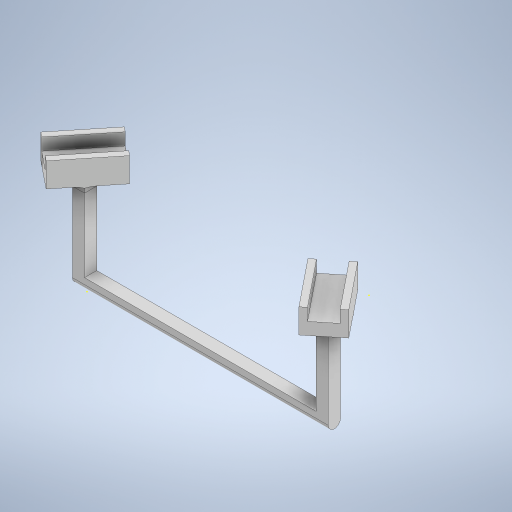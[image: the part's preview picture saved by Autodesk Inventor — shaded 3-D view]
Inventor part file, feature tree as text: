
AUTODESK INVENTOR PART (.ipt)
format: ipt  version: 2023 (Build 270158000, 158)  size: 727,040 bytes
history: native  units: in
note: dims shown in document units (in); Inventor stores cm internally (conversion verified against a paired STEP export)
features: sketch x13, extrude x10, fillet x2
ambient origin geometry x8: Origin, YZ Plane, XZ Plane, XY Plane, X Axis, Y Axis, Z Axis, Center Point
bodies: Solid1 (feature_tree)
feature tree (25):
  extrude  "Extrusion1"  Depth=0.25in
  fillet  "Fillet1"  Radius=1.75in
  extrude  "Extrusion2"  Depth=5.25in
  sketch  "Sketch4"  dims[d6=0.25in d7=0.0in d8=0.125in]
  sketch  "Sketch5"  dims[d11=0.25in d12=0.0in d32=0.0625in d33=0.0in]
  extrude  "Extrusion3"  Depth=0.125in
  extrude  "Extrusion4"  Depth=0.25in TaperAngle=0.0deg
  extrude  "Extrusion5"  Depth=0.0625in TaperAngle=0.0deg
  extrude  "Extrusion6"  Depth=0.5in
  sketch  "Sketch10"  dims[d48=0.125in d49=0.0in d50=0.25in]
  extrude  "Extrusion7"  Depth=0.125in TaperAngle=0.0deg
  extrude  "Extrusion8"  Depth=0.125in TaperAngle=0.0deg
  extrude  "Extrusion9"  Depth=0.25in
  extrude  "Extrusion10"  TaperAngle=0.0deg  [1 undecoded]
  fillet  "Fillet4"  Radius=0.5in
  sketch  "Sketch1"  dims[d1=2.0in d2=0.25in d3=1.75in]
  sketch  "Sketch2"  dims[d4=4.75in d5=5.25in]
  sketch  "Sketch6"  dims[d34=0.0625in d35=0.0in d36=0.0625in d37=0.0in]
  sketch  "Sketch7"  dims[d38=0.0625in d39=0.0in d40=0.5in]
  sketch  "Sketch8"  dims[d41=0.125in d42=0.0in d43=0.125in d44=0.0in]
  sketch  "Sketch9"  dims[d45=0.5in d46=0.125in d47=0.0in]
  sketch  "Sketch11"  dims[d9=0.0in d10=0.0in d27=0.5in]
  sketch  "Sketch12"  dims[d28=0.0344in]
  sketch  "Sketch13"  dims[d29=0.5in]
  sketch  "Sketch14"  dims[d30=0.0344in]
note: 1 required parameter value undecoded (feature->parameter linkage not recoverable at this tier; creation-order binding heuristic only, values carry confidence <= 0.55)
